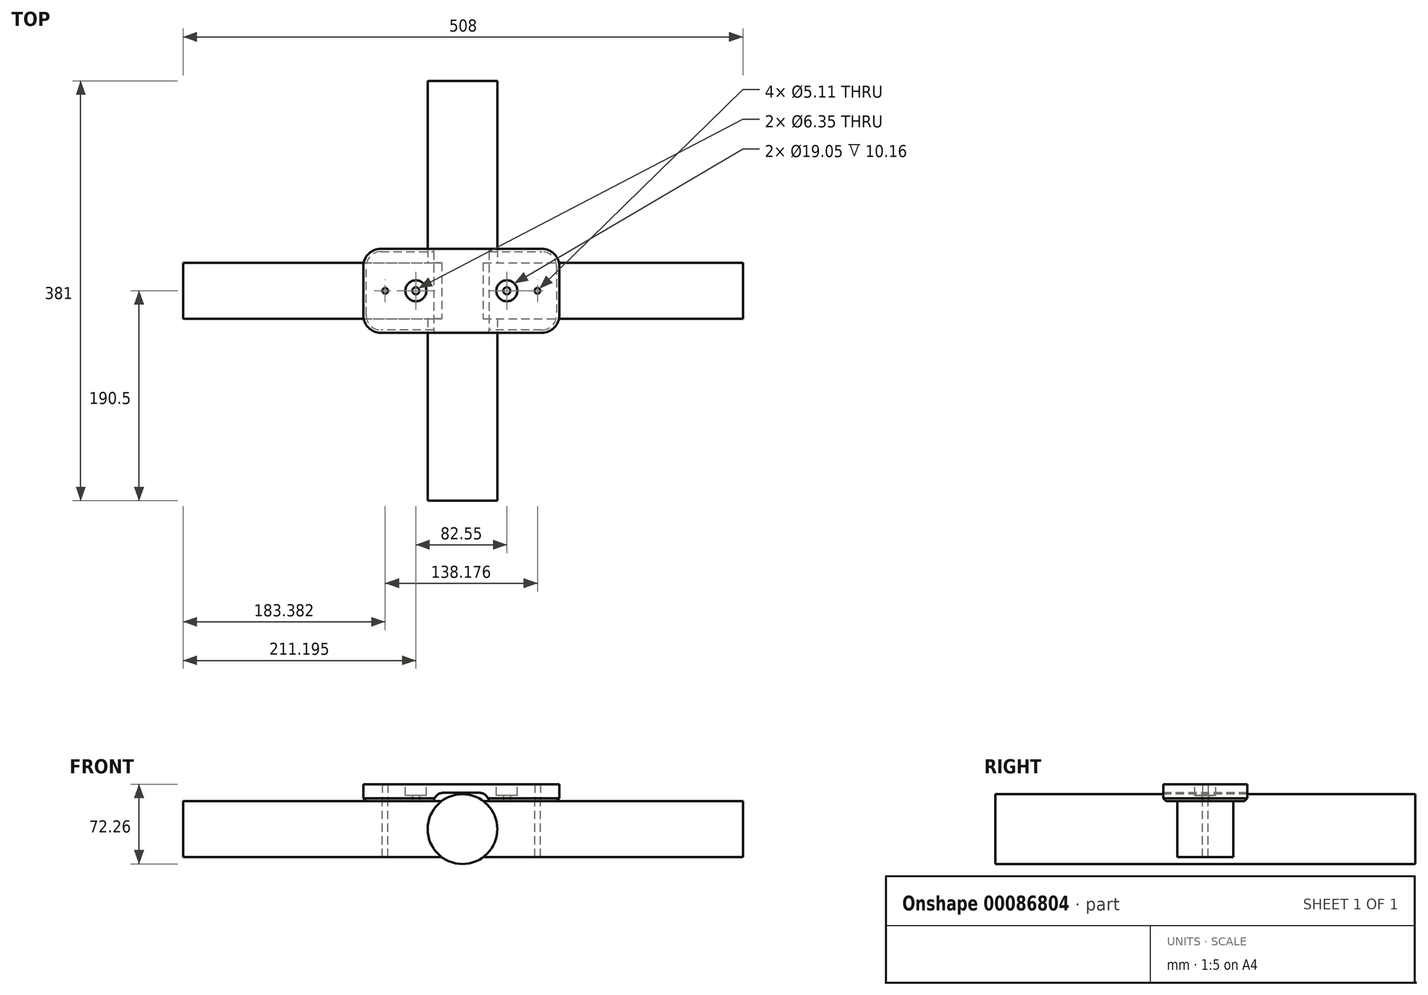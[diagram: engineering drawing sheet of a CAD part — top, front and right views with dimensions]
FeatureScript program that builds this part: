
annotation { "Feature Type Name" : "Feature", "Feature Type Description" : "" }
export const myFeature = defineFeature(function(context is Context, id is Id, definition is map)
    precondition{}
    {
        {
            var Q0;
            Q0=qCreatedBy(makeId("Top.planeOp"),FACE);
            var sketch = newSketch(context, id + "F0", { "sketchPlane" : qUnion([Q0])});
            skLineSegment(sketch, "E0.bottom", {"start": v(15.88, 0) * mm, "end": v(161.92, 0) * mm});
            skLineSegment(sketch, "E0.top", {"start": v(15.88, 76.2) * mm, "end": v(161.92, 76.2) * mm});
            skLineSegment(sketch, "E0.left", {"start": v(0, 15.87) * mm, "end": v(0, 60.32) * mm});
            skLineSegment(sketch, "E0.right", {"start": v(177.8, 15.88) * mm, "end": v(177.8, 60.33) * mm});
            skLineSegment(sketch, "E1", {"start": v(0, 38.1) * mm, "end": v(177.8, 38.1) * mm, "construction": true});
            skCircle(sketch, "E2", {"center": v(19.81, 38.1) * mm, "radius": 2.55 * mm});
            skCircle(sketch, "E3", {"center": v(157.99, 38.1) * mm, "radius": 2.55 * mm});
            skLineSegment(sketch, "E4", {"start": v(88.9, 76.2) * mm, "end": v(88.9, 0) * mm, "construction": true});
            skPoint(sketch, "E5.visualSharp", {"position": v(0, 76.2) * mm});
            skArc(sketch, "E5.filletArc", {"start": v(15.88, 76.2) * mm, "mid": v(4.65, 71.55) * mm, "end": v(0, 60.32) * mm});
            skPoint(sketch, "E6.visualSharp", {"position": v(177.8, 76.2) * mm});
            skArc(sketch, "E6.filletArc", {"start": v(177.8, 60.33) * mm, "mid": v(173.15, 71.55) * mm, "end": v(161.92, 76.2) * mm});
            skPoint(sketch, "E7.visualSharp", {"position": v(177.8, 0) * mm});
            skArc(sketch, "E7.filletArc", {"start": v(161.92, 0) * mm, "mid": v(173.15, 4.65) * mm, "end": v(177.8, 15.88) * mm});
            skPoint(sketch, "E8.visualSharp", {"position": v(0, 0) * mm});
            skArc(sketch, "E8.filletArc", {"start": v(0, 15.87) * mm, "mid": v(4.65, 4.65) * mm, "end": v(15.88, 0) * mm});
            skCircle(sketch, "E9", {"center": v(47.62, 38.1) * mm, "radius": 3.18 * mm});
            skCircle(sketch, "E10", {"center": v(130.17, 38.1) * mm, "radius": 3.18 * mm});
            skSolve(sketch);
        }
        {
            var Q0;
            Q0 = qSketchRegion(id + "F0", true);
            extrude(context, id + "F1", {"entities" : qUnion([Q0]), "depth" : 15.24 * mm});
        }
        {
            var Q0;
            Q0=makeQuery(id+"F1.opExtrude","SWEPT_FACE",FACE,{"disambiguationData":[OSD([sQuery(id+"F0.wireOp",EDGE,"E0.bottom")])]});
            var sketch = newSketch(context, id + "F2", { "sketchPlane" : qUnion([Q0])});
            skLineSegment(sketch, "E11", {"start": v(88.9, 15.24) * mm, "end": v(88.9, 0) * mm, "construction": true});
            skLineSegment(sketch, "E12.bottom", {"start": v(73.02, 7.62) * mm, "end": v(104.77, 7.62) * mm});
            skLineSegment(sketch, "E12.top", {"start": v(63.5, -16) * mm, "end": v(114.3, -16) * mm});
            skLineSegment(sketch, "E12.left", {"start": v(63.5, -1.9) * mm, "end": v(63.5, -16) * mm});
            skLineSegment(sketch, "E12.right", {"start": v(114.3, -1.9) * mm, "end": v(114.3, -16) * mm});
            skPoint(sketch, "E13.visualSharp", {"position": v(63.5, 7.62) * mm});
            skArc(sketch, "E13.filletArc", {"start": v(73.02, 7.62) * mm, "mid": v(66.29, 4.83) * mm, "end": v(63.5, -1.9) * mm});
            skPoint(sketch, "E14.visualSharp", {"position": v(114.3, 7.62) * mm});
            skArc(sketch, "E14.filletArc", {"start": v(114.3, -1.9) * mm, "mid": v(111.51, 4.83) * mm, "end": v(104.77, 7.62) * mm});
            skSolve(sketch);
        }
        {
            var Q0;
            Q0 = qSketchRegion(id + "F2", true);
            extrude(context, id + "F3", {"entities" : qUnion([Q0]), "operationType" : NewBodyOperationType.REMOVE, "endBound" : BoundingType.THROUGH_ALL, "oppositeDirection" : true, "depth" : 25.4 * mm});
        }
        {
            var Q0;
            {var subQ0=sQuery(id+"F0.wireOp",EDGE,"E0.bottom");var subQ1=sQuery(id+"F0.wireOp",EDGE,"E8.filletArc");Q0=makeQuery(id+"F3.boolean.opBoolean","SPLIT",EDGE,{"disambiguationData":[TD([makeQuery(id+"F1.opExtrude","SWEPT_FACE",FACE,{"disambiguationData":[OSD([subQ1])]})])],"derivedFrom":makeQuery(id+"F1.opExtrude","CAP_EDGE",EDGE,{"disambiguationData":[OSD([subQ0])],"isStart":true})});}
            var Q1;
            Q1=makeQuery(id+"F1.opExtrude","CAP_EDGE",EDGE,{"disambiguationData":[OSD([sQuery(id+"F0.wireOp",EDGE,"E8.filletArc")])],"isStart":true});
            var Q2;
            Q2=makeQuery(id+"F1.opExtrude","CAP_EDGE",EDGE,{"disambiguationData":[OSD([sQuery(id+"F0.wireOp",EDGE,"E0.left")])],"isStart":true});
            var Q3;
            Q3=makeQuery(id+"F1.opExtrude","CAP_EDGE",EDGE,{"disambiguationData":[OSD([sQuery(id+"F0.wireOp",EDGE,"E5.filletArc")])],"isStart":true});
            var Q4;
            {var subQ0=sQuery(id+"F0.wireOp",EDGE,"E5.filletArc");var subQ1=sQuery(id+"F0.wireOp",EDGE,"E0.top");Q4=makeQuery(id+"F3.boolean.opBoolean","SPLIT",EDGE,{"disambiguationData":[TD([makeQuery(id+"F1.opExtrude","SWEPT_FACE",FACE,{"disambiguationData":[OSD([subQ0])]})])],"derivedFrom":makeQuery(id+"F1.opExtrude","CAP_EDGE",EDGE,{"disambiguationData":[OSD([subQ1])],"isStart":true})});}
            var Q5;
            {var subQ0=sQuery(id+"F0.wireOp",EDGE,"E6.filletArc");var subQ1=sQuery(id+"F0.wireOp",EDGE,"E0.top");Q5=makeQuery(id+"F3.boolean.opBoolean","SPLIT",EDGE,{"disambiguationData":[TD([makeQuery(id+"F1.opExtrude","SWEPT_FACE",FACE,{"disambiguationData":[OSD([subQ0])]})])],"derivedFrom":makeQuery(id+"F1.opExtrude","CAP_EDGE",EDGE,{"disambiguationData":[OSD([subQ1])],"isStart":true})});}
            var Q6;
            Q6=makeQuery(id+"F1.opExtrude","CAP_EDGE",EDGE,{"disambiguationData":[OSD([sQuery(id+"F0.wireOp",EDGE,"E6.filletArc")])],"isStart":true});
            var Q7;
            Q7=makeQuery(id+"F1.opExtrude","CAP_EDGE",EDGE,{"disambiguationData":[OSD([sQuery(id+"F0.wireOp",EDGE,"E0.right")])],"isStart":true});
            var Q8;
            Q8=makeQuery(id+"F1.opExtrude","CAP_EDGE",EDGE,{"disambiguationData":[OSD([sQuery(id+"F0.wireOp",EDGE,"E7.filletArc")])],"isStart":true});
            var Q9;
            {var subQ0=sQuery(id+"F0.wireOp",EDGE,"E0.bottom");var subQ1=sQuery(id+"F0.wireOp",EDGE,"E7.filletArc");Q9=makeQuery(id+"F3.boolean.opBoolean","SPLIT",EDGE,{"disambiguationData":[TD([makeQuery(id+"F1.opExtrude","SWEPT_FACE",FACE,{"disambiguationData":[OSD([subQ1])]})])],"derivedFrom":makeQuery(id+"F1.opExtrude","CAP_EDGE",EDGE,{"disambiguationData":[OSD([subQ0])],"isStart":true})});}
            chamfer(context, id + "F4", {"entities" : qUnion([Q0, Q1, Q2, Q3, Q4, Q5, Q6, Q7, Q8, Q9]), "width" : 2.54 * mm, "tangentPropagation" : true});
        }
        {
            var Q0;
            {var subQ0=sQuery(id+"F0.wireOp",EDGE,"E2");var subQ1=sQuery(id+"F0.wireOp",EDGE,"E0.left");var subQ2=sQuery(id+"F0.wireOp",EDGE,"E0.top");var subQ3=sQuery(id+"F0.wireOp",EDGE,"E0.bottom");var subQ4=sQuery(id+"F0.wireOp",EDGE,"E5.filletArc");var subQ5=sQuery(id+"F0.wireOp",EDGE,"E8.filletArc");Q0=makeQuery(id+"F3.boolean.opBoolean","SPLIT",FACE,{"disambiguationData":[TD([makeQuery(id+"F1.opExtrude","SWEPT_FACE",FACE,{"disambiguationData":[OSD([subQ1])]})])],"derivedFrom":makeQuery(id+"F1.opExtrude","CAP_FACE",FACE,{"disambiguationData":[OSD([subQ3,subQ2,subQ1,sQuery(id+"F0.wireOp",EDGE,"E0.right"),subQ0,sQuery(id+"F0.wireOp",EDGE,"E3"),subQ4,sQuery(id+"F0.wireOp",EDGE,"E6.filletArc"),sQuery(id+"F0.wireOp",EDGE,"E7.filletArc"),subQ5])],"isStart":true})});}
            var sketch = newSketch(context, id + "F5", { "sketchPlane" : qUnion([Q0])});
            skLineSegment(sketch, "E15.bottom", {"start": v(-163.57, -12.7) * mm, "end": v(344.43, -12.7) * mm});
            skLineSegment(sketch, "E15.top", {"start": v(-163.57, -63.5) * mm, "end": v(344.43, -63.5) * mm});
            skLineSegment(sketch, "E15.left", {"start": v(-163.57, -12.7) * mm, "end": v(-163.57, -63.5) * mm});
            skLineSegment(sketch, "E15.right", {"start": v(344.43, -12.7) * mm, "end": v(344.43, -63.5) * mm});
            skCircle(sketch, "E16", {"center": v(19.81, -38.1) * mm, "radius": 2.55 * mm});
            skCircle(sketch, "E17", {"center": v(157.99, -38.1) * mm, "radius": 2.55 * mm});
            skSolve(sketch);
        }
        {
            var Q0;
            Q0 = qSketchRegion(id + "F5", true);
            extrude(context, id + "F6", {"entities" : qUnion([Q0]), "depth" : 50.8 * mm});
        }
        {
            var Q0;
            {var subQ2=sQuery(id+"F5.wireOp",EDGE,"E15.right");var subQ4=sQuery(id+"F5.wireOp",EDGE,"E15.top");Q0=makeQuery(id+"FOeCuCfMhqGxBHO_2.boolean.opBoolean","SPLIT",FACE,{"disambiguationData":[TD([makeQuery(id+"F6.opExtrude","SWEPT_FACE",FACE,{"disambiguationData":[OSD([subQ2])]})])],"derivedFrom":makeQuery(id+"F6.opExtrude","SWEPT_FACE",FACE,{"disambiguationData":[OSD([subQ4])]})});}
            cPlane(context, id + "F7", {"entities" : qUnion([Q0]), "cplaneType" : CPlaneType.OFFSET, "offset" : 25.4 * mm, "oppositeDirection" : true, "width" : 152.4 * mm, "height" : 152.4 * mm});
        }
        {
            var Q0;
            Q0=qCreatedBy(id+"F7.planeOp",FACE);
            var sketch = newSketch(context, id + "F8", { "sketchPlane" : qUnion([Q0])});
            skLineSegment(sketch, "E18", {"start": v(162.55, -25.4) * mm, "end": v(-345.45, -25.4) * mm, "construction": true});
            skLineSegment(sketch, "E19.0", {"start": v(-89.92, 12.7) * mm, "end": v(-89.92, 0) * mm, "construction": true});
            skCircle(sketch, "E20", {"center": v(-89.92, -25.4) * mm, "radius": 31.62 * mm});
            skSolve(sketch);
        }
        {
            var Q0;
            Q0 = qSketchRegion(id + "F8", true);
            extrude(context, id + "F9", {"entities" : qUnion([Q0]), "operationType" : NewBodyOperationType.ADD, "endBound" : BoundingType.SYMMETRIC, "depth" : 381 * mm});
        }
        {
            var Q0;
            Q0=makeQuery(id+"F1.opExtrude","CAP_FACE",FACE,{"disambiguationData":[OSD([sQuery(id+"F0.wireOp",EDGE,"E0.bottom"),sQuery(id+"F0.wireOp",EDGE,"E0.top"),sQuery(id+"F0.wireOp",EDGE,"E0.left"),sQuery(id+"F0.wireOp",EDGE,"E0.right"),sQuery(id+"F0.wireOp",EDGE,"E2"),sQuery(id+"F0.wireOp",EDGE,"E3"),sQuery(id+"F0.wireOp",EDGE,"E5.filletArc"),sQuery(id+"F0.wireOp",EDGE,"E6.filletArc"),sQuery(id+"F0.wireOp",EDGE,"E7.filletArc"),sQuery(id+"F0.wireOp",EDGE,"E8.filletArc"),sQuery(id+"F0.wireOp",EDGE,"E9"),sQuery(id+"F0.wireOp",EDGE,"E10")])],"isStart":false});
            var sketch = newSketch(context, id + "F10", { "sketchPlane" : qUnion([Q0])});
            skCircle(sketch, "E21", {"center": v(130.17, 38.1) * mm, "radius": 9.53 * mm});
            skCircle(sketch, "E22", {"center": v(47.62, 38.1) * mm, "radius": 9.53 * mm});
            skSolve(sketch);
        }
        {
            var Q0;
            Q0 = qSketchRegion(id + "F10", true);
            extrude(context, id + "F11", {"entities" : qUnion([Q0]), "operationType" : NewBodyOperationType.REMOVE, "oppositeDirection" : true, "depth" : 10.16 * mm});
        }
    });
